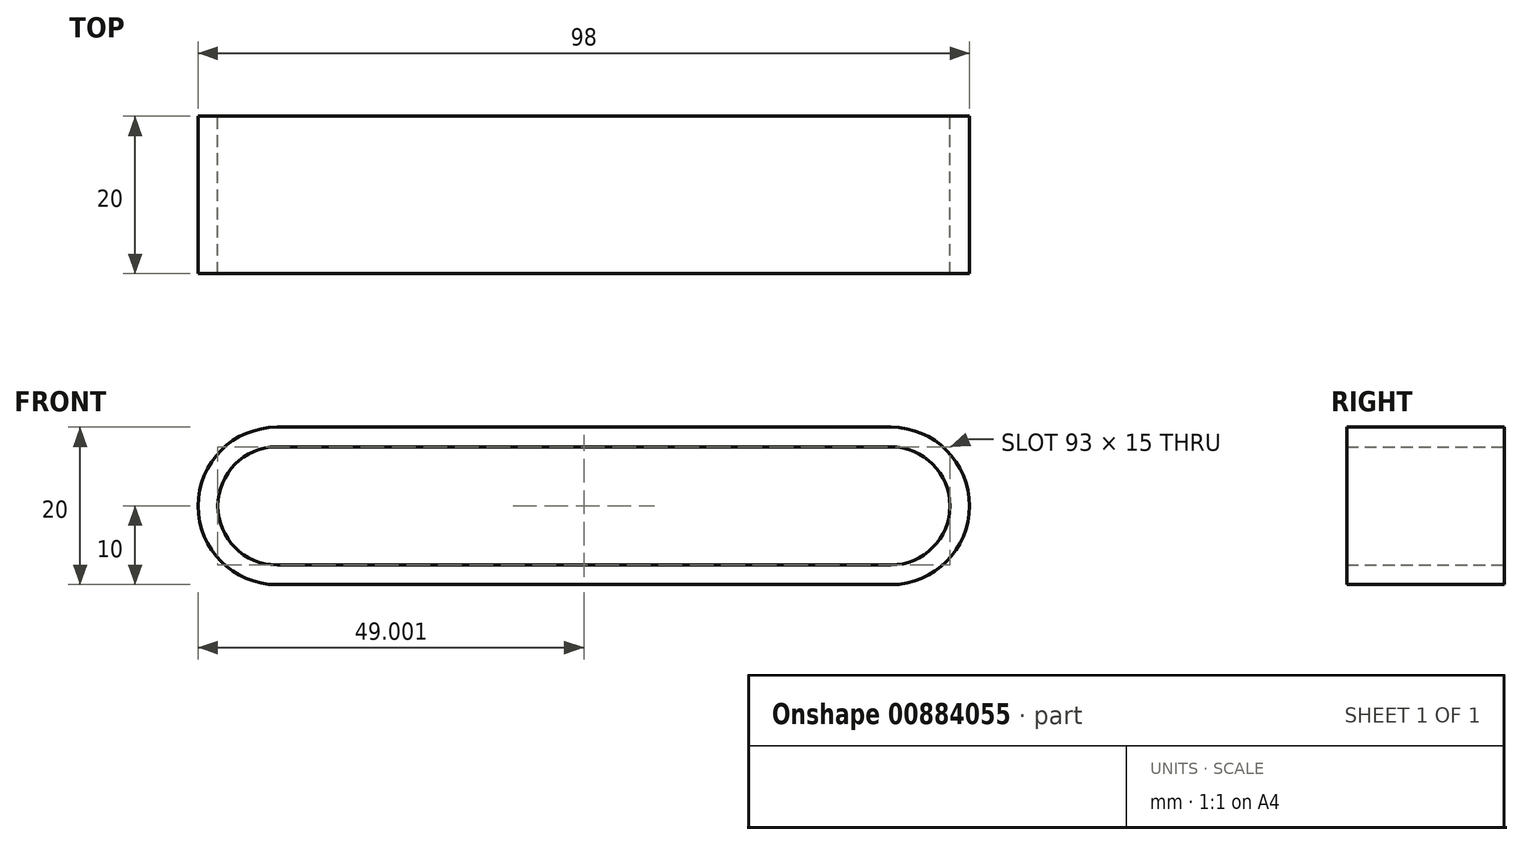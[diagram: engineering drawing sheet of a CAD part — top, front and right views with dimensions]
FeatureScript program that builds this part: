
annotation { "Feature Type Name" : "Feature", "Feature Type Description" : "" }
export const myFeature = defineFeature(function(context is Context, id is Id, definition is map)
    precondition{}
    {
        {
            var Q0;
            Q0=qCreatedBy(makeId("Front.planeOp"),FACE);
            var sketch = newSketch(context, id + "F0", { "sketchPlane" : qUnion([Q0])});
            skLineSegment(sketch, "E0", {"start": v(-7.96, 0) * mm, "end": v(70.04, 0) * mm});
            skLineSegment(sketch, "E1", {"start": v(70.04, 2.5) * mm, "end": v(-7.96, 2.5) * mm});
            skLineSegment(sketch, "E2", {"start": v(-7.96, 17.5) * mm, "end": v(70.04, 17.5) * mm});
            skLineSegment(sketch, "E3", {"start": v(70.04, 20) * mm, "end": v(-7.96, 20) * mm});
            skArc(sketch, "E4", {"start": v(-7.96, 2.5) * mm, "mid": v(-15.46, 10) * mm, "end": v(-7.96, 17.5) * mm});
            skArc(sketch, "E5", {"start": v(-7.96, 20) * mm, "mid": v(-17.96, 10) * mm, "end": v(-7.96, 0) * mm});
            skArc(sketch, "E6", {"start": v(70.04, 2.5) * mm, "mid": v(77.54, 10) * mm, "end": v(70.04, 17.5) * mm});
            skArc(sketch, "E7", {"start": v(70.04, 0) * mm, "mid": v(80.04, 10) * mm, "end": v(70.04, 20) * mm});
            skSolve(sketch);
        }
        {
            var Q0;
            Q0=makeQuery(id+"F0.imprint","IMPRINT",FACE,{"disambiguationData":[TD([[makeQuery(id+"F0.imprint","IMPRINT",EDGE,{"derivedFrom":sQuery(id+"F0.wireOp",EDGE,"E0")}),1.0]])]});
            extrude(context, id + "F1", {"entities" : qUnion([Q0]), "depth" : 20 * mm, "offsetDistance" : 25 * mm});
        }
    });
